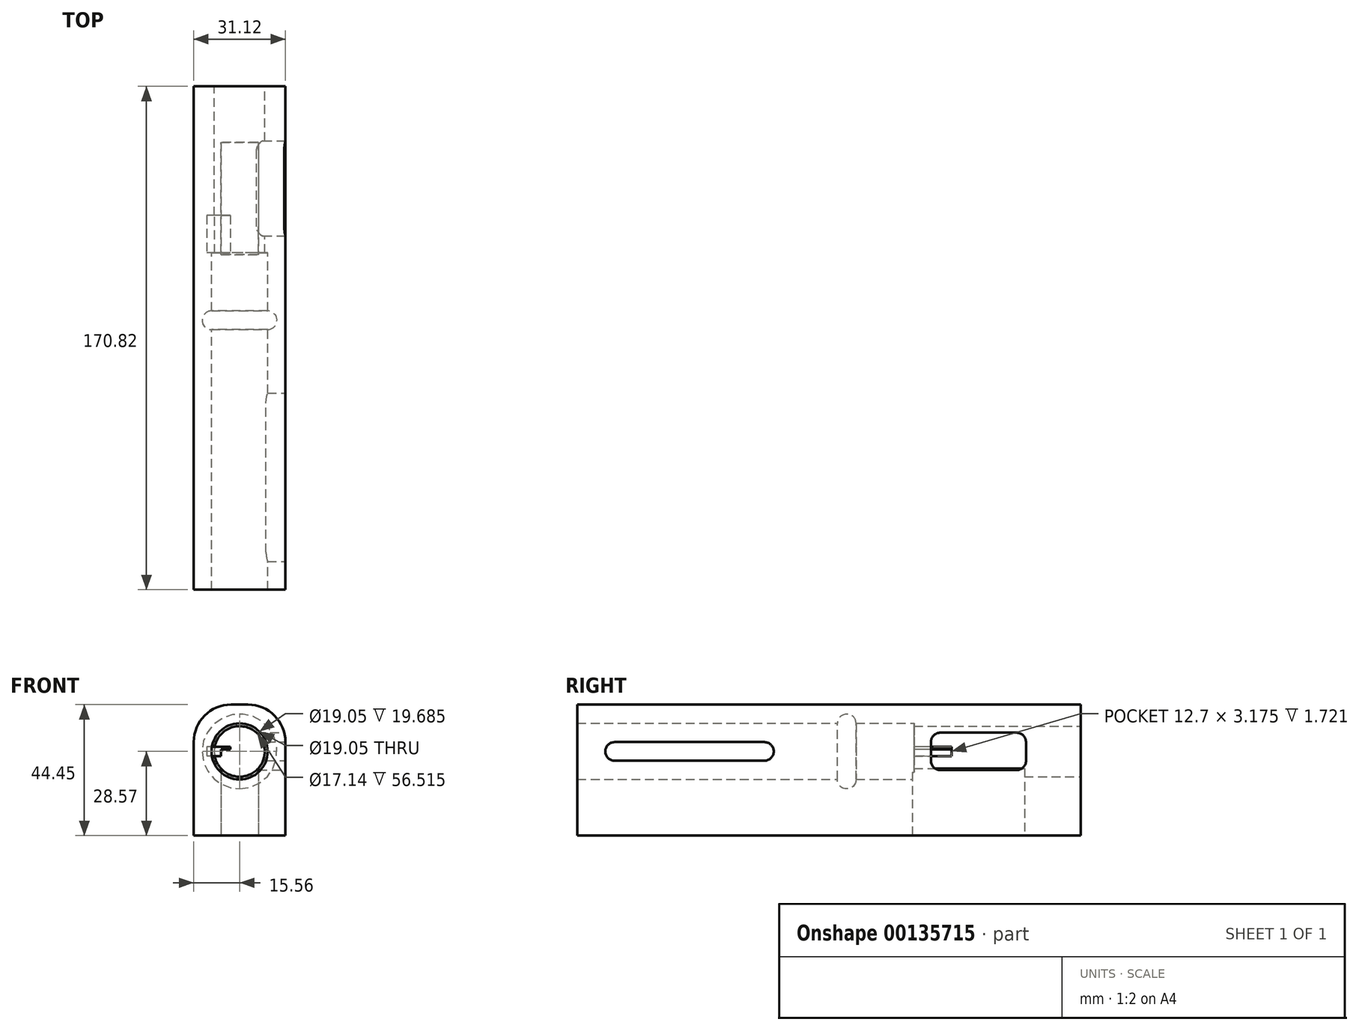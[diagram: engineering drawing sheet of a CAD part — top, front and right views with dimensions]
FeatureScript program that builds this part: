
annotation { "Feature Type Name" : "Feature", "Feature Type Description" : "" }
export const myFeature = defineFeature(function(context is Context, id is Id, definition is map)
    precondition{}
    {
        {
            var Q0;
            Q0=qCreatedBy(makeId("Front.planeOp"),FACE);
            var sketch = newSketch(context, id + "F0", { "sketchPlane" : qUnion([Q0])});
            skCircle(sketch, "E0", {"center": v(0, 0) * mm, "radius": 9.53 * mm});
            skLineSegment(sketch, "E1.bottom", {"start": v(-2.86, 15.88) * mm, "end": v(2.86, 15.88) * mm});
            skLineSegment(sketch, "E1.top", {"start": v(-15.56, -28.58) * mm, "end": v(15.56, -28.58) * mm});
            skLineSegment(sketch, "E1.left", {"start": v(-15.56, 3.18) * mm, "end": v(-15.56, -28.58) * mm});
            skLineSegment(sketch, "E1.right", {"start": v(15.56, 3.17) * mm, "end": v(15.56, -28.58) * mm});
            skPoint(sketch, "E1.middle", {"position": v(0, -6.35) * mm});
            skPoint(sketch, "E2.visualSharp", {"position": v(15.56, 15.88) * mm});
            skArc(sketch, "E2.filletArc", {"start": v(15.56, 3.17) * mm, "mid": v(11.84, 12.16) * mm, "end": v(2.86, 15.88) * mm});
            skPoint(sketch, "E3.visualSharp", {"position": v(-15.56, 15.88) * mm});
            skArc(sketch, "E3.filletArc", {"start": v(-2.86, 15.88) * mm, "mid": v(-11.84, 12.16) * mm, "end": v(-15.56, 3.18) * mm});
            skCircle(sketch, "E4", {"center": v(0, 0) * mm, "radius": 8.57 * mm});
            skSolve(sketch);
        }
        {
            var Q0;
            Q0=makeQuery(id+"F0.imprint","IMPRINT",FACE,{"disambiguationData":[TD([[makeQuery(id+"F0.imprint","IMPRINT",EDGE,{"derivedFrom":sQuery(id+"F0.wireOp",EDGE,"E0")}),-1.0]])]});
            extrude(context, id + "F1", {"entities" : qUnion([Q0]), "offsetDistance" : 25.4 * mm, "depth" : 170.8 * mm});
        }
        {
            var Q0;
            Q0=makeQuery(id+"F0.imprint","IMPRINT",FACE,{"disambiguationData":[TD([[makeQuery(id+"F0.imprint","IMPRINT",EDGE,{"derivedFrom":sQuery(id+"F0.wireOp",EDGE,"E0")}),1.0]])]});
            extrude(context, id + "F2", {"entities" : qUnion([Q0]), "operationType" : NewBodyOperationType.ADD, "flatOperationType" : FlatOperationType.REMOVE, "offsetDistance" : 25.4 * mm, "depth" : 56.52 * mm, "domain" : OperationDomain.MODEL});
        }
        {
            var Q0;
            Q0=makeQuery(id+"F1.opExtrude","SWEPT_FACE",FACE,{"disambiguationData":[OSD([sQuery(id+"F0.wireOp",EDGE,"E1.right")])]});
            var sketch = newSketch(context, id + "F3", { "sketchPlane" : qUnion([Q0])});
            skLineSegment(sketch, "E5.bottom", {"start": v(-47.63, 6.35) * mm, "end": v(-21.72, 6.35) * mm});
            skLineSegment(sketch, "E5.top", {"start": v(-47.63, -6.35) * mm, "end": v(-21.72, -6.35) * mm});
            skLineSegment(sketch, "E5.left", {"start": v(-50.8, 3.18) * mm, "end": v(-50.8, -3.18) * mm});
            skPoint(sketch, "E5.middle", {"position": v(0, 0) * mm});
            skLineSegment(sketch, "E6", {"start": v(-18.54, 3.18) * mm, "end": v(-18.54, -3.18) * mm});
            skPoint(sketch, "E7.visualSharp", {"position": v(-50.8, 6.35) * mm});
            skArc(sketch, "E7.filletArc", {"start": v(-47.63, 6.35) * mm, "mid": v(-49.87, 5.42) * mm, "end": v(-50.8, 3.18) * mm});
            skPoint(sketch, "E8.visualSharp", {"position": v(-18.54, 6.35) * mm});
            skArc(sketch, "E8.filletArc", {"start": v(-18.54, 3.18) * mm, "mid": v(-19.47, 5.42) * mm, "end": v(-21.72, 6.35) * mm});
            skPoint(sketch, "E9.visualSharp", {"position": v(-18.54, -6.35) * mm});
            skArc(sketch, "E9.filletArc", {"start": v(-21.72, -6.35) * mm, "mid": v(-19.47, -5.42) * mm, "end": v(-18.54, -3.18) * mm});
            skPoint(sketch, "E10.visualSharp", {"position": v(-50.8, -6.35) * mm});
            skArc(sketch, "E10.filletArc", {"start": v(-50.8, -3.18) * mm, "mid": v(-49.87, -5.42) * mm, "end": v(-47.63, -6.35) * mm});
            skSolve(sketch);
        }
        {
            var Q0;
            Q0=makeQuery(id+"F3.imprint","IMPRINT",FACE,{"disambiguationData":[TD([[makeQuery(id+"F3.imprint","IMPRINT",EDGE,{"derivedFrom":sQuery(id+"F3.wireOp",EDGE,"E5.bottom")}),-1.0]])]});
            var Q1;
            Q1=makeQuery(id+"F3.imprint","IMPRINT",FACE,{"disambiguationData":[TD([[makeQuery(id+"F3.imprint","IMPRINT",EDGE,{"derivedFrom":sQuery(id+"F3.wireOp",EDGE,"E5.top")}),1.0]])]});
            extrude(context, id + "F4", {"entities" : qUnion([Q0, Q1]), "operationType" : NewBodyOperationType.REMOVE, "oppositeDirection" : true, "depth" : 19.05 * mm});
        }
        {
            var Q0;
            Q0=makeQuery(id+"F2.opExtrude","CAP_FACE",FACE,{"disambiguationData":[OSD([sQuery(id+"F0.wireOp",EDGE,"E0"),sQuery(id+"F0.wireOp",EDGE,"E4")])],"isStart":false});
            var sketch = newSketch(context, id + "F5", { "sketchPlane" : qUnion([Q0])});
            skLineSegment(sketch, "E11.bottom", {"start": v(-3.1, 1.59) * mm, "end": v(-11.11, 1.59) * mm});
            skLineSegment(sketch, "E11.top", {"start": v(-3.1, -1.59) * mm, "end": v(-11.11, -1.59) * mm});
            skLineSegment(sketch, "E11.left", {"start": v(-3.1, 1.59) * mm, "end": v(-3.1, -1.59) * mm});
            skPoint(sketch, "E11.middle", {"position": v(-8.57, 0) * mm});
            skLineSegment(sketch, "E12", {"start": v(-11.11, 1.59) * mm, "end": v(-11.11, -1.59) * mm});
            skPoint(sketch, "E13", {"position": v(-8.42, 1.59) * mm});
            skPoint(sketch, "E14", {"position": v(-8.42, -1.59) * mm});
            skSolve(sketch);
        }
        {
            var Q0;
            {var subQ0=sQuery(id+"F5.wireOp",EDGE,"E11.bottom");var subQ1=makeQuery(id+"F2.opExtrude","CAP_EDGE",EDGE,{"disambiguationData":[OSD([sQuery(id+"F0.wireOp",EDGE,"E0")])],"isStart":false});var subQ2=makeQuery(id+"F5.imprint","INTERSECT",VERTEX,{"derivedFrom":[subQ1,subQ0]});Q0=makeQuery(id+"F5.imprint","IMPRINT",FACE,{"disambiguationData":[TD([[makeQuery(id+"F5.imprint","IMPRINT",EDGE,{"disambiguationData":[TD([[subQ2,1.0]])],"derivedFrom":subQ0}),1.0]])]});}
            extrude(context, id + "F6", {"entities" : qUnion([Q0]), "operationType" : NewBodyOperationType.REMOVE, "oppositeDirection" : true, "depth" : 12.7 * mm});
        }
        {
            var Q0;
            Q0 = qSketchRegion(id + "F5", true);
            extrude(context, id + "F7", {"entities" : qUnion([Q0]), "oppositeDirection" : true, "depth" : 12.7 * mm});
        }
        {
            var Q0;
            Q0=qCreatedBy(makeId("Right.planeOp"),FACE);
            var sketch = newSketch(context, id + "F8", { "sketchPlane" : qUnion([Q0])});
            skLineSegment(sketch, "E15.left", {"start": v(-76.2, 9.53) * mm, "end": v(-76.2, 0) * mm});
            skLineSegment(sketch, "E15.right", {"start": v(-82.55, 9.53) * mm, "end": v(-82.55, 0) * mm});
            skArc(sketch, "E16", {"start": v(-76.2, 9.53) * mm, "mid": v(-79.38, 12.7) * mm, "end": v(-82.55, 9.53) * mm});
            skLineSegment(sketch, "E17", {"start": v(-76.2, 0) * mm, "end": v(-82.55, 0) * mm});
            skSolve(sketch);
        }
        {
            var Q0;
            Q0=makeQuery(id+"F8.imprint","IMPRINT",FACE,{"disambiguationData":[TD([[makeQuery(id+"F8.imprint","IMPRINT",EDGE,{"derivedFrom":sQuery(id+"F8.wireOp",EDGE,"E15.left")}),-1.0]])]});
            var Q1;
            Q1=sQuery(id+"F8.wireOp",EDGE,"E17");
            revolve(context, id + "F9", {"operationType" : NewBodyOperationType.REMOVE, "entities" : qUnion([Q0]), "axis" : qUnion([Q1]), "revolveType" : RevolveType.FULL, "oppositeDirection" : true});
        }
        {
            var Q0;
            Q0=makeQuery(id+"F1.opExtrude","SWEPT_FACE",FACE,{"disambiguationData":[OSD([sQuery(id+"F0.wireOp",EDGE,"E1.right")])]});
            var sketch = newSketch(context, id + "F10", { "sketchPlane" : qUnion([Q0])});
            skLineSegment(sketch, "E18.bottom", {"start": v(-107.31, 3.18) * mm, "end": v(-158.12, 3.18) * mm});
            skLineSegment(sketch, "E18.top", {"start": v(-107.31, -3.18) * mm, "end": v(-158.12, -3.18) * mm});
            skPoint(sketch, "E19", {"position": v(-158.12, 3.17) * mm});
            skPoint(sketch, "E20", {"position": v(-158.12, -3.17) * mm});
            skArc(sketch, "E21", {"start": v(-107.31, -3.17) * mm, "mid": v(-104.14, 0) * mm, "end": v(-107.31, 3.18) * mm});
            skArc(sketch, "E22", {"start": v(-158.12, 3.17) * mm, "mid": v(-161.3, 0) * mm, "end": v(-158.12, -3.18) * mm});
            skSolve(sketch);
        }
        {
            var Q0;
            {var subQ0=sQuery(id+"F10.wireOp",EDGE,"E18.bottom");Q0=makeQuery(id+"F10.imprint","IMPRINT",FACE,{"disambiguationData":[TD([[makeQuery(id+"F10.imprint","IMPRINT",EDGE,{"derivedFrom":subQ0}),1.0]])]});}
            var Q1;
            {var subQ0=sQuery(id+"F10.wireOp",EDGE,"E18.top");Q1=makeQuery(id+"F10.imprint","IMPRINT",FACE,{"disambiguationData":[TD([[makeQuery(id+"F10.imprint","IMPRINT",EDGE,{"derivedFrom":subQ0}),-1.0]])]});}
            extrude(context, id + "F11", {"entities" : qUnion([Q0, Q1]), "operationType" : NewBodyOperationType.REMOVE, "oppositeDirection" : true, "depth" : 12.7 * mm});
        }
        {
            var Q0;
            Q0=makeQuery(id+"F1.opExtrude","SWEPT_FACE",FACE,{"disambiguationData":[OSD([sQuery(id+"F0.wireOp",EDGE,"E1.top")])]});
            var sketch = newSketch(context, id + "F12", { "sketchPlane" : qUnion([Q0])});
            skLineSegment(sketch, "E23", {"start": v(0, 0) * mm, "end": v(0, 19.05) * mm});
            skLineSegment(sketch, "E24.bottom", {"start": v(6.35, 19.05) * mm, "end": v(-6.35, 19.05) * mm});
            skLineSegment(sketch, "E24.top", {"start": v(6.35, 57.15) * mm, "end": v(-6.35, 57.15) * mm});
            skLineSegment(sketch, "E24.left", {"start": v(6.35, 19.05) * mm, "end": v(6.35, 57.15) * mm});
            skLineSegment(sketch, "E24.right", {"start": v(-6.35, 19.05) * mm, "end": v(-6.35, 57.15) * mm});
            skPoint(sketch, "E24.middle", {"position": v(0, 38.1) * mm});
            skLineSegment(sketch, "E25.trimOffspring", {"start": v(0, 57.15) * mm, "end": v(0, 170.81) * mm});
            skSolve(sketch);
        }
        {
            var Q0;
            {var subQ0=sQuery(id+"F12.wireOp",EDGE,"E24.left");Q0=makeQuery(id+"F12.imprint","IMPRINT",FACE,{"disambiguationData":[TD([[makeQuery(id+"F12.imprint","IMPRINT",EDGE,{"derivedFrom":subQ0}),1.0]])]});}
            extrude(context, id + "F13", {"entities" : qUnion([Q0]), "operationType" : NewBodyOperationType.REMOVE, "oppositeDirection" : true, "depth" : 29.2 * mm});
        }
    });
